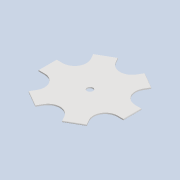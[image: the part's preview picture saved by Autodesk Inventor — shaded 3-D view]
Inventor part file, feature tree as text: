
AUTODESK INVENTOR PART (.ipt)
format: ipt  version: 2020 (Build 240168000, 168)  size: 128,000 bytes
history: native  units: mm
features: extrude x3, sketch x3, pattern_circular x1, fillet x1
ambient origin geometry x8: Origin, YZ Plane, XZ Plane, XY Plane, X Axis, Y Axis, Z Axis, Center Point
bodies: Solid1 (feature_tree)
feature tree (8):
  extrude  "Extrusion1"  Depth=0.2mm TaperAngle=0.0deg
  extrude  "Extrusion2"  Depth=0.1mm
  pattern_circular  "Circular Pattern1"  [2 undecoded]
  extrude  "Extrusion3"  Depth=2.0mm TaperAngle=360.0deg
  fillet  "Fillet1"  Radius=1.0mm
  sketch  "Sketch1"  dims[d0=3.0mm d1=0.2mm d2=0.0mm]
  sketch  "Sketch2"  dims[d3=0.1mm d4=7.0mm]
  sketch  "Sketch3"  dims[d5=0.2mm d6=3.0mm d7=0.0mm d8=60.0mm d9=360.0deg d11=1.0mm d12=1.0mm d13=0.0mm d14=2.0mm]
note: 2 required parameter values undecoded (feature->parameter linkage not recoverable at this tier; creation-order binding heuristic only, values carry confidence <= 0.55)
